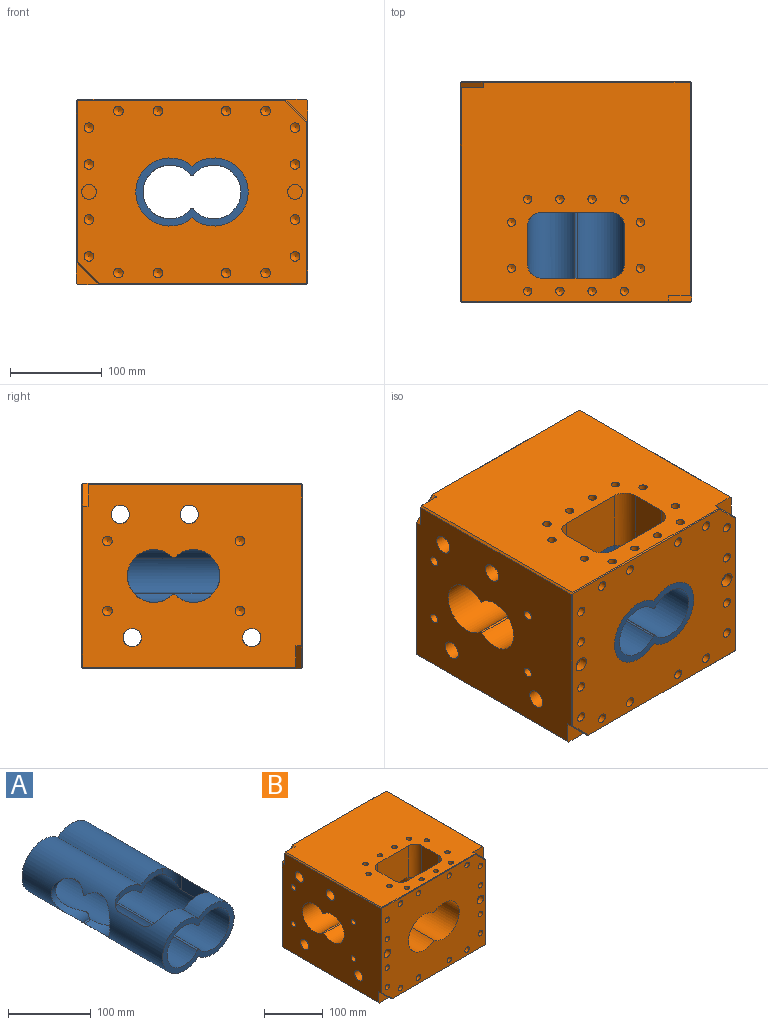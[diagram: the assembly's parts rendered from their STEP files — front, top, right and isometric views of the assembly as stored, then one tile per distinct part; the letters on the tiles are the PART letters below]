
ASSEMBLY  parts=2 mates=1
PART A: 21 faces, bbox 122x240x74 mm
  f0: cylinder r=2mm len=26mm, axis (0,1,0), area 91.5mm2, adj f1,f5,f7,f19
  f1: cylinder r=29.15mm len=240mm, axis (0,1,0), area 23609.6mm2, adj f0,f4,f6,f7,f8,f9,f10,f11
  f2: cylinder r=37mm len=240mm, axis (0,1,0), area 30974.5mm2, adj f3,f7,f8,f9,f10,f11,f12,f13
  f3: cylinder r=37mm len=240mm, axis (0,1,0), area 36307mm2, adj f2,f7,f8,f16,f17,f18,f19,f20
  f4: cylinder r=2mm len=142mm, axis (0,1,0), area 499.6mm2, adj f1,f5,f8,f18
  f5: cylinder r=29.15mm len=240mm, axis (0,1,0), area 29669.7mm2, adj f0,f4,f6,f7,f8,f16,f17,f18
  f6: cylinder r=2mm len=240mm, axis (0,1,0), area 844.4mm2, adj f1,f5,f7,f8
  f7: plane 122x74mm, normal (0,-1,0), area 2474.6mm2, adj f0,f1,f2,f3,f5,f6
  f8: plane 122x74mm, normal (0,1,0), area 2474.6mm2, adj f1,f2,f3,f4,f5,f6
  f9: cylinder r=2mm len=10.47mm, axis (-1,0,0), area 30.9mm2, adj f1,f2,f10,f12
  f10: cylinder r=28.75mm len=57.5mm, axis (-1,0,0), area 1649.5mm2, adj f1,f2,f9,f11
  f11: cylinder r=2mm len=10.47mm, axis (-1,0,0), area 30.9mm2, adj f1,f2,f10,f12
  f12: cylinder r=28.75mm len=57.5mm, axis (-1,0,0), area 1648.8mm2, adj f1,f2,f9,f11
  f13: cylinder r=16mm len=31.69mm, axis (0,0,1), area 322.6mm2, adj f1,f2,f14,f18
  f14: plane 40x20.03mm, normal (1,0,0), area 801mm2, adj f1,f2,f13,f15
  f15: cylinder r=16mm len=31.69mm, axis (0,0,1), area 322.6mm2, adj f1,f2,f14,f19
  f16: plane 40x20.03mm, normal (-1,0,0), area 801mm2, adj f3,f5,f17,f20
  f17: cylinder r=16mm len=31.69mm, axis (0,0,1), area 322.6mm2, adj f3,f5,f16,f18
  f18: plane 74x19.14mm, normal (0,-1,0), area 631.5mm2, adj f1,f2,f3,f4,f5,f13,f17
  f19: plane 74x19.14mm, normal (0,1,0), area 631.5mm2, adj f0,f1,f2,f3,f5,f15,f20
  f20: cylinder r=16mm len=31.69mm, axis (0,0,1), area 322.6mm2, adj f3,f5,f16,f19
PART B: 156 faces, bbox 252x240x202 mm
  f0: plane 238x198mm, normal (1,0,0), area 45591.4mm2, adj f88,f89,f90,f91,f134,f135,f138,f139
  f1: plane 250x200mm, normal (0,1,0), area 40031.3mm2, adj f5,f7,f45,f47,f49,f51,f53,f55
  f2: plane 248x238mm, normal (0,0,1), area 50572.3mm2, adj f100,f101,f102,f103,f104,f105,f106,f107
  f3: plane 250x200mm, normal (0,-1,0), area 40031.3mm2, adj f5,f7,f9,f11,f13,f15,f17,f19
  f4: plane 248x238mm, normal (0,0,-1), area 58457mm2, adj f83,f132,f133,f138,f139,f140,f142,f145
  f5: cylinder r=37mm len=240mm, axis (0,1,0), area 30974.5mm2, adj f1,f3,f7,f84,f85,f86,f87,f103
  f6: plane 238x198mm, normal (-1,0,0), area 40429.2mm2, adj f84,f85,f86,f87,f88,f89,f90,f91
  f7: cylinder r=37mm len=240mm, axis (0,1,0), area 36307mm2, adj f1,f3,f5,f100,f101,f102,f103,f107
  f8: cone r=0mm half-angle=59deg, axis (0,-1,0), area 101mm2, adj f9
  f9: cylinder r=5.25mm len=21mm, axis (0,-1,0), area 692.7mm2, adj f3,f8
  f10: cone r=0mm half-angle=59deg, axis (0,-1,0), area 101mm2, adj f11
  f11: cylinder r=5.25mm len=21mm, axis (0,-1,0), area 692.7mm2, adj f3,f10
  f12: cone r=0mm half-angle=59deg, axis (0,-1,0), area 101mm2, adj f13
  f13: cylinder r=5.25mm len=21mm, axis (0,-1,0), area 692.7mm2, adj f3,f12
  f14: cone r=0mm half-angle=59deg, axis (0,-1,0), area 101mm2, adj f15
  f15: cylinder r=5.25mm len=21mm, axis (0,-1,0), area 692.7mm2, adj f3,f14
  f16: cone r=0mm half-angle=59deg, axis (0,-1,0), area 101mm2, adj f17
  f17: cylinder r=5.25mm len=21mm, axis (0,-1,0), area 692.7mm2, adj f3,f16
  f18: cone r=0mm half-angle=59deg, axis (0,-1,0), area 101mm2, adj f19
  f19: cylinder r=5.25mm len=21mm, axis (0,-1,0), area 692.7mm2, adj f3,f18
  f20: cone r=0mm half-angle=59deg, axis (0,-1,0), area 101mm2, adj f21
  f21: cylinder r=5.25mm len=21mm, axis (0,-1,0), area 692.7mm2, adj f3,f20
  f22: cone r=0mm half-angle=59deg, axis (0,-1,0), area 101mm2, adj f23
  f23: cylinder r=5.25mm len=21mm, axis (0,-1,0), area 692.7mm2, adj f3,f22
  f24: cone r=0mm half-angle=59deg, axis (0,-1,0), area 101mm2, adj f25
  f25: cylinder r=5.25mm len=21mm, axis (0,-1,0), area 692.7mm2, adj f3,f24
  f26: cone r=0mm half-angle=59deg, axis (0,-1,0), area 101mm2, adj f27
  f27: cylinder r=5.25mm len=21mm, axis (0,-1,0), area 692.7mm2, adj f3,f26
  f28: cone r=0mm half-angle=59deg, axis (0,-1,0), area 101mm2, adj f29
  f29: cylinder r=5.25mm len=21mm, axis (0,-1,0), area 692.7mm2, adj f3,f28
  f30: cone r=0mm half-angle=59deg, axis (0,-1,0), area 101mm2, adj f31
  f31: cylinder r=5.25mm len=21mm, axis (0,-1,0), area 692.7mm2, adj f3,f30
  f32: cone r=0mm half-angle=59deg, axis (0,-1,0), area 101mm2, adj f33
  f33: cylinder r=5.25mm len=21mm, axis (0,-1,0), area 692.7mm2, adj f3,f32
  f34: cone r=0mm half-angle=59deg, axis (0,-1,0), area 101mm2, adj f35
  f35: cylinder r=5.25mm len=21mm, axis (0,-1,0), area 692.7mm2, adj f3,f34
  f36: cone r=0mm half-angle=59deg, axis (0,-1,0), area 101mm2, adj f37
  f37: cylinder r=5.25mm len=21mm, axis (0,-1,0), area 692.7mm2, adj f3,f36
  f38: cone r=0mm half-angle=59deg, axis (0,-1,0), area 101mm2, adj f39
  f39: cylinder r=5.25mm len=21mm, axis (0,-1,0), area 692.7mm2, adj f3,f38
  f40: cylinder r=8mm len=16mm, axis (0,-1,0), area 502.7mm2, adj f3,f41
  f41: plane 16x16mm, normal (0,-1,0), area 201.1mm2, adj f40
  f42: cylinder r=8mm len=16mm, axis (0,-1,0), area 502.7mm2, adj f3,f43
  f43: plane 16x16mm, normal (0,-1,0), area 201.1mm2, adj f42
  f44: cone r=0mm half-angle=59deg, axis (0,1,0), area 101mm2, adj f45
  f45: cylinder r=5.25mm len=21mm, axis (0,1,0), area 692.7mm2, adj f1,f44
  f46: cone r=0mm half-angle=59deg, axis (0,1,0), area 101mm2, adj f47
  f47: cylinder r=5.25mm len=21mm, axis (0,1,0), area 692.7mm2, adj f1,f46
  f48: cone r=0mm half-angle=59deg, axis (0,1,0), area 101mm2, adj f49
  f49: cylinder r=5.25mm len=21mm, axis (0,1,0), area 692.7mm2, adj f1,f48
  f50: cone r=0mm half-angle=59deg, axis (0,1,0), area 101mm2, adj f51
  f51: cylinder r=5.25mm len=21mm, axis (0,1,0), area 692.7mm2, adj f1,f50
  f52: cone r=0mm half-angle=59deg, axis (0,1,0), area 101mm2, adj f53
  f53: cylinder r=5.25mm len=21mm, axis (0,1,0), area 692.7mm2, adj f1,f52
  f54: cone r=0mm half-angle=59deg, axis (0,1,0), area 101mm2, adj f55
  f55: cylinder r=5.25mm len=21mm, axis (0,1,0), area 692.7mm2, adj f1,f54
  f56: cone r=0mm half-angle=59deg, axis (0,1,0), area 101mm2, adj f57
  f57: cylinder r=5.25mm len=21mm, axis (0,1,0), area 692.7mm2, adj f1,f56
  f58: cone r=0mm half-angle=59deg, axis (0,1,0), area 101mm2, adj f59
  f59: cylinder r=5.25mm len=21mm, axis (0,1,0), area 692.7mm2, adj f1,f58
  f60: cone r=0mm half-angle=59deg, axis (0,1,0), area 101mm2, adj f61
  f61: cylinder r=5.25mm len=21mm, axis (0,1,0), area 692.7mm2, adj f1,f60
  f62: cone r=0mm half-angle=59deg, axis (0,1,0), area 101mm2, adj f63
  f63: cylinder r=5.25mm len=21mm, axis (0,1,0), area 692.7mm2, adj f1,f62
  f64: cone r=0mm half-angle=59deg, axis (0,1,0), area 101mm2, adj f65
  f65: cylinder r=5.25mm len=21mm, axis (0,1,0), area 692.7mm2, adj f1,f64
  f66: cone r=0mm half-angle=59deg, axis (0,1,0), area 101mm2, adj f67
  f67: cylinder r=5.25mm len=21mm, axis (0,1,0), area 692.7mm2, adj f1,f66
  f68: cone r=0mm half-angle=59deg, axis (0,1,0), area 101mm2, adj f69
  f69: cylinder r=5.25mm len=21mm, axis (0,1,0), area 692.7mm2, adj f1,f68
  f70: cone r=0mm half-angle=59deg, axis (0,1,0), area 101mm2, adj f71
  f71: cylinder r=5.25mm len=21mm, axis (0,1,0), area 692.7mm2, adj f1,f70
  f72: cone r=0mm half-angle=59deg, axis (0,1,0), area 101mm2, adj f73
  f73: cylinder r=5.25mm len=21mm, axis (0,1,0), area 692.7mm2, adj f1,f72
  f74: cone r=0mm half-angle=59deg, axis (0,1,0), area 101mm2, adj f75
  f75: cylinder r=5.25mm len=21mm, axis (0,1,0), area 692.7mm2, adj f1,f74
  f76: cylinder r=8mm len=16mm, axis (0,1,0), area 502.7mm2, adj f1,f77
  f77: plane 16x16mm, normal (0,1,0), area 201.1mm2, adj f76
  f78: cylinder r=8mm len=16mm, axis (0,1,0), area 502.7mm2, adj f1,f79
  f79: plane 16x16mm, normal (0,1,0), area 201.1mm2, adj f78
  f80: cone r=0mm half-angle=59deg, axis (0,0,-1), area 44.9mm2, adj f81
  f81: cylinder r=3.5mm len=47mm, axis (0,0,-1), area 1033.6mm2, adj f80,f82
  f82: plane 19.25x19.25mm, normal (0,0,-1), area 252.6mm2, adj f81,f83
  f83: cylinder r=9.62mm len=19.25mm, axis (0,0,-1), area 1028.1mm2, adj f4,f82
  f84: cylinder r=2mm len=71.23mm, axis (-1,0,0), area 219.9mm2, adj f5,f6,f85,f87
  f85: cylinder r=28.75mm len=78.71mm, axis (-1,0,0), area 9831.7mm2, adj f5,f6,f84,f86
  f86: cylinder r=2mm len=71.23mm, axis (-1,0,0), area 219.9mm2, adj f5,f6,f85,f87
  f87: cylinder r=28.75mm len=78.71mm, axis (-1,0,0), area 9831.6mm2, adj f5,f6,f84,f86
  f88: cylinder r=10mm len=252mm, axis (-1,0,0), area 15833.6mm2, adj f0,f6
  f89: cylinder r=10mm len=252mm, axis (-1,0,0), area 15833.6mm2, adj f0,f6
  f90: cylinder r=10mm len=252mm, axis (-1,0,0), area 15833.6mm2, adj f0,f6
  f91: cylinder r=10mm len=252mm, axis (-1,0,0), area 15833.6mm2, adj f0,f6
  f92: cone r=0mm half-angle=59deg, axis (-1,0,0), area 101mm2, adj f93
  f93: cylinder r=5.25mm len=22.5mm, axis (-1,0,0), area 742.2mm2, adj f6,f92
  f94: cone r=0mm half-angle=59deg, axis (-1,0,0), area 101mm2, adj f95
  f95: cylinder r=5.25mm len=22.5mm, axis (-1,0,0), area 742.2mm2, adj f6,f94
  f96: cone r=0mm half-angle=59deg, axis (-1,0,0), area 101mm2, adj f97
  f97: cylinder r=5.25mm len=22.5mm, axis (-1,0,0), area 742.2mm2, adj f6,f96
  f98: cone r=0mm half-angle=59deg, axis (-1,0,0), area 101mm2, adj f99
  f99: cylinder r=5.25mm len=22.5mm, axis (-1,0,0), area 742.2mm2, adj f6,f98
  f100: plane 78.02x40mm, normal (-1,0,0), area 3120.9mm2, adj f2,f7,f101,f102
  f101: cylinder r=16mm len=78.02mm, axis (0,0,1), area 1830.8mm2, adj f2,f7,f100,f103
  f102: cylinder r=16mm len=78.02mm, axis (0,0,1), area 1830.8mm2, adj f2,f7,f100,f107
  f103: plane 74x72.84mm, normal (0,-1,0), area 4890.1mm2, adj f2,f5,f7,f101,f104
  f104: cylinder r=16mm len=78.02mm, axis (0,0,1), area 1830.8mm2, adj f2,f5,f103,f105
  f105: plane 78.02x40mm, normal (1,0,0), area 3120.9mm2, adj f2,f5,f104,f106
  f106: cylinder r=16mm len=78.02mm, axis (0,0,1), area 1830.8mm2, adj f2,f5,f105,f107
  f107: plane 74x72.84mm, normal (0,1,0), area 4890.1mm2, adj f2,f5,f7,f102,f106
  f108: cone r=0mm half-angle=59deg, axis (0,0,1), area 74.2mm2, adj f109
  f109: cylinder r=4.5mm len=21mm, axis (0,0,1), area 593.8mm2, adj f2,f108
  f110: cone r=0mm half-angle=59deg, axis (0,0,1), area 74.2mm2, adj f111
  f111: cylinder r=4.5mm len=21mm, axis (0,0,1), area 593.8mm2, adj f2,f110
  f112: cone r=0mm half-angle=59deg, axis (0,0,1), area 74.2mm2, adj f113
  f113: cylinder r=4.5mm len=21mm, axis (0,0,1), area 593.8mm2, adj f2,f112
  f114: cone r=0mm half-angle=59deg, axis (0,0,1), area 74.2mm2, adj f115
  f115: cylinder r=4.5mm len=21mm, axis (0,0,1), area 593.8mm2, adj f2,f114
  f116: cone r=0mm half-angle=59deg, axis (0,0,1), area 74.2mm2, adj f117
  f117: cylinder r=4.5mm len=21mm, axis (0,0,1), area 593.8mm2, adj f2,f116
  f118: cone r=0mm half-angle=59deg, axis (0,0,1), area 74.2mm2, adj f119
  f119: cylinder r=4.5mm len=21mm, axis (0,0,1), area 593.8mm2, adj f2,f118
  f120: cone r=0mm half-angle=59deg, axis (0,0,1), area 74.2mm2, adj f121
  f121: cylinder r=4.5mm len=21mm, axis (0,0,1), area 593.8mm2, adj f2,f120
  f122: cone r=0mm half-angle=59deg, axis (0,0,1), area 74.2mm2, adj f123
  f123: cylinder r=4.5mm len=21mm, axis (0,0,1), area 593.8mm2, adj f2,f122
  f124: cone r=0mm half-angle=59deg, axis (0,0,1), area 74.2mm2, adj f125
  f125: cylinder r=4.5mm len=21mm, axis (0,0,1), area 593.8mm2, adj f2,f124
  f126: cone r=0mm half-angle=59deg, axis (0,0,1), area 74.2mm2, adj f127
  f127: cylinder r=4.5mm len=21mm, axis (0,0,1), area 593.8mm2, adj f2,f126
  f128: cone r=0mm half-angle=59deg, axis (0,0,1), area 74.2mm2, adj f129
  f129: cylinder r=4.5mm len=21mm, axis (0,0,1), area 593.8mm2, adj f2,f128
  f130: cone r=0mm half-angle=59deg, axis (0,0,1), area 74.2mm2, adj f131
  f131: cylinder r=4.5mm len=21mm, axis (0,0,1), area 593.8mm2, adj f2,f130
  f132: plane 25x25mm, normal (-0.71,0,-0.71), area 212.1mm2, adj f4,f6,f133,f154
  f133: plane 25x25mm, normal (0,-1,0), area 310.5mm2, adj f4,f6,f132,f140
  f134: plane 25x25mm, normal (0.71,0,0.71), area 212.1mm2, adj f0,f2,f135,f151
  f135: plane 25x25mm, normal (0,-1,0), area 310.5mm2, adj f0,f2,f134,f143
  f136: plane 25x25mm, normal (-0.71,0,0.71), area 212.1mm2, adj f2,f6,f137,f149
  f137: plane 25x25mm, normal (0,1,0), area 310.5mm2, adj f2,f6,f136,f141
  f138: plane 25x25mm, normal (0.71,0,-0.71), area 212.1mm2, adj f0,f4,f139,f146
  f139: plane 25x25mm, normal (0,1,0), area 310.5mm2, adj f0,f4,f138,f142
  f140: plane 233x2mm, normal (-0.71,0,-0.71), area 657.6mm2, adj f4,f6,f133,f145,f148
  f141: plane 233x2mm, normal (-0.71,0,0.71), area 657.6mm2, adj f2,f6,f137,f150,f153
  f142: plane 233x2mm, normal (0.71,0,-0.71), area 657.6mm2, adj f0,f4,f139,f152,f155
  f143: plane 233x2mm, normal (0.71,0,0.71), area 657.6mm2, adj f0,f2,f135,f144,f147
  f144: plane 176x1mm, normal (0.71,0.71,0), area 247.9mm2, adj f0,f1,f143,f146
  f145: plane 226x1mm, normal (0,0.71,-0.71), area 318.6mm2, adj f1,f4,f140,f146
  f146: plane 25.41x25.41mm, normal (0.5,0.71,-0.5), area 49.4mm2, adj f1,f138,f144,f145
  f147: plane 226x1mm, normal (0,0.71,0.71), area 318.6mm2, adj f1,f2,f143,f149
  f148: plane 176x1mm, normal (-0.71,0.71,0), area 247.9mm2, adj f1,f6,f140,f149
  f149: plane 25.41x25.41mm, normal (-0.5,0.71,0.5), area 49.4mm2, adj f1,f136,f147,f148
  f150: plane 226x1mm, normal (0,-0.71,0.71), area 318.6mm2, adj f2,f3,f141,f151
  f151: plane 25.41x25.41mm, normal (0.5,-0.71,0.5), area 49.4mm2, adj f3,f134,f150,f152
  f152: plane 176x1mm, normal (0.71,-0.71,0), area 247.9mm2, adj f0,f3,f142,f151
  f153: plane 176x1mm, normal (-0.71,-0.71,0), area 247.9mm2, adj f3,f6,f141,f154
  f154: plane 25.41x25.41mm, normal (-0.5,-0.71,-0.5), area 49.4mm2, adj f3,f132,f153,f155
  f155: plane 226x1mm, normal (0,-0.71,-0.71), area 318.6mm2, adj f3,f4,f142,f154
PLACE A at identity
PLACE B at identity fixed
MATE fastened A.f5 <-> B.f7  axis (0,-1,0) through (24,-36,0)mm
